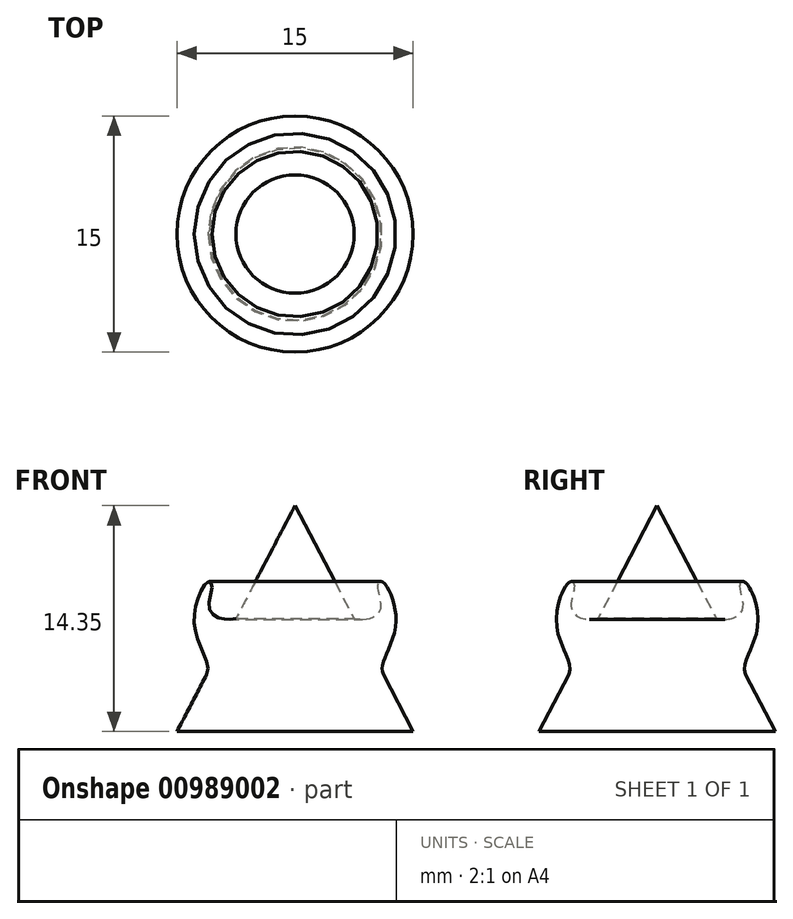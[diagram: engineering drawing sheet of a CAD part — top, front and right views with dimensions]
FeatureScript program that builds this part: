
annotation { "Feature Type Name" : "Feature", "Feature Type Description" : "" }
export const myFeature = defineFeature(function(context is Context, id is Id, definition is map)
    precondition{}
    {
        {
            var Q0;
            Q0=qCreatedBy(makeId("Front.planeOp"),FACE);
            var sketch = newSketch(context, id + "F0", { "sketchPlane" : qUnion([Q0])});
            skLineSegment(sketch, "E0", {"start": v(0, 0) * mm, "end": v(-7.5, 0) * mm});
            skLineSegment(sketch, "E1", {"start": v(-7.5, 0) * mm, "end": v(-5.61, 3.61) * mm});
            skLineSegment(sketch, "E2", {"start": v(0, 0) * mm, "end": v(0, 55.25) * mm, "construction": true});
            skLineSegment(sketch, "E3", {"start": v(0, 0) * mm, "end": v(0, 14.35) * mm});
            skPoint(sketch, "E4.1.internal.snap0", {"position": v(-3.75, 7.18) * mm});
            skFitSpline(sketch, "E4", {"points": [v(-3.75, 7.18) * mm, v(-4.7, 7.18) * mm, v(-5.45, 7.83) * mm, v(-5.27, 9.28) * mm, v(-5.5, 9.52) * mm, v(-6.1, 8.63) * mm, v(-6.4, 6.75) * mm, v(-5.83, 4.98) * mm, v(-5.61, 3.61) * mm], "startDerivative": vector(-8.82, -1.13) * mm, "endDerivative": vector(-4.49, -8.58) * mm});
            skLineSegment(sketch, "E5.trimOffspring", {"start": v(-3.75, 7.18) * mm, "end": v(0, 14.35) * mm});
            skSolve(sketch);
        }
        {
            var Q0;
            Q0 = qSketchRegion(id + "F0", true);
            var Q1;
            Q1=sQuery(id+"F0.wireOp",EDGE,"E3");
            revolve(context, id + "F1", {"surfaceOperationType" : NewSurfaceOperationType.NEW, "entities" : qUnion([Q0]), "axis" : qUnion([Q1]), "revolveType" : RevolveType.FULL});
        }
    });
